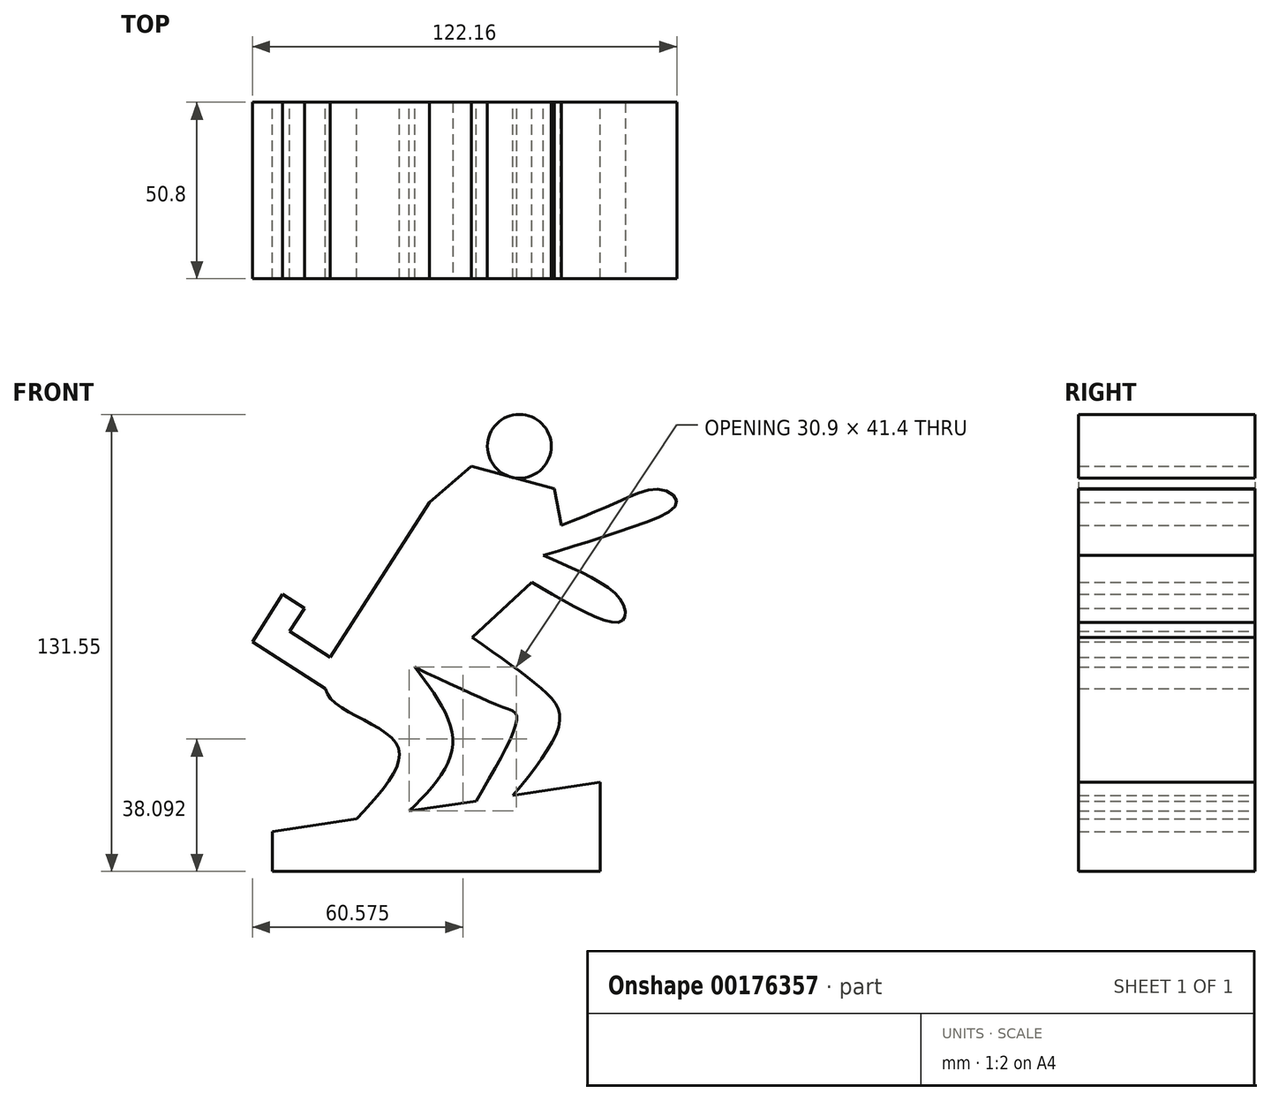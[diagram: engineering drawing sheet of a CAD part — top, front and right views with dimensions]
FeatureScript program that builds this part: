
annotation { "Feature Type Name" : "Feature", "Feature Type Description" : "" }
export const myFeature = defineFeature(function(context is Context, id is Id, definition is map)
    precondition{}
    {
        {
            var Q0;
            Q0=qCreatedBy(makeId("Front.planeOp"),FACE);
            var sketch = newSketch(context, id + "F0", { "sketchPlane" : qUnion([Q0])});
            skCircle(sketch, "E0", {"center": v(25.9, 46.62) * mm, "radius": 9.18 * mm});
            skLineSegment(sketch, "E1", {"start": v(12.09, 40.87) * mm, "end": v(35.96, 34.37) * mm});
            skLineSegment(sketch, "E2", {"start": v(12.09, 40.87) * mm, "end": v(0, 30.5) * mm});
            skLineSegment(sketch, "E3", {"start": v(0, 30.5) * mm, "end": v(-28.5, -14.1) * mm});
            skLineSegment(sketch, "E4", {"start": v(35.96, 34.37) * mm, "end": v(38, 23.89) * mm});
            skLineSegment(sketch, "E5", {"start": v(38, 23.89) * mm, "end": v(32.8, 15.25) * mm});
            skLineSegment(sketch, "E6", {"start": v(18.42, 23.89) * mm, "end": v(14.68, 15.25) * mm});
            skLineSegment(sketch, "E7", {"start": v(29.44, 7.54) * mm, "end": v(11.83, -8.81) * mm});
            skFitSpline(sketch, "E8", {"points": [v(-28.5, -14.1) * mm, v(-28.5, -25.9) * mm, v(-9.2, -39.43) * mm, v(-21.87, -61.62) * mm], "startDerivative": vector(-16.56, -48.93) * mm, "endDerivative": vector(-61.45, -65.14) * mm});
            skFitSpline(sketch, "E9", {"points": [v(18.42, 23.89) * mm, v(32.8, 15.25) * mm, v(54.97, 2.6) * mm, v(54.97, -3.84) * mm, v(29.44, 7.54) * mm, v(14.68, 15.25) * mm], "startDerivative": vector(63.22, -43.87) * mm, "endDerivative": vector(-62.95, 30.16) * mm});
            skFitSpline(sketch, "E10", {"points": [v(38, 23.89) * mm, v(53.97, 30.5) * mm, v(66.63, 34.22) * mm, v(71.24, 30.5) * mm, v(60.01, 23.89) * mm, v(32.8, 15.25) * mm], "startDerivative": vector(74.59, 29.4) * mm, "endDerivative": vector(-100.82, -30.07) * mm});
            skFitSpline(sketch, "E11", {"points": [v(0, 0) * mm, v(31.52, -22.48) * mm, v(37.56, -32.27) * mm, v(21.44, -57.02) * mm], "startDerivative": vector(88.18, -59.65) * mm, "endDerivative": vector(-64.62, -77.15) * mm});
            skFitSpline(sketch, "E12", {"points": [v(-13.67, -12.4) * mm, v(21.44, -28.52) * mm, v(25.19, -31.11) * mm, v(12.52, -57.02) * mm], "startDerivative": vector(94.72, -45.41) * mm, "endDerivative": vector(-50.43, -85.1) * mm});
            skFitSpline(sketch, "E13", {"points": [v(-4.18, -16.95) * mm, v(6.76, -39.43) * mm, v(-9.2, -61.62) * mm], "startDerivative": vector(35.42, -46.75) * mm, "endDerivative": vector(-44.95, -42.74) * mm});
            skLineSegment(sketch, "E14", {"start": v(-28.5, -14.1) * mm, "end": v(-40.17, -6.64) * mm});
            skLineSegment(sketch, "E15", {"start": v(-40.17, -6.64) * mm, "end": v(-35.93, 0) * mm});
            skLineSegment(sketch, "E16", {"start": v(-35.93, 0) * mm, "end": v(-42.2, 4.01) * mm});
            skLineSegment(sketch, "E17", {"start": v(-42.2, 4.01) * mm, "end": v(-50.92, -9.64) * mm});
            skLineSegment(sketch, "E18", {"start": v(-50.92, -9.64) * mm, "end": v(-29.91, -23.13) * mm});
            skLineSegment(sketch, "E19", {"start": v(-29.91, -23.13) * mm, "end": v(-32.1, -21.9) * mm});
            skLineSegment(sketch, "E20", {"start": v(-45.14, -64.27) * mm, "end": v(49.2, -50.06) * mm});
            skLineSegment(sketch, "E21", {"start": v(-45.14, -64.27) * mm, "end": v(-45.14, -75.74) * mm});
            skLineSegment(sketch, "E22", {"start": v(-45.14, -75.74) * mm, "end": v(49.2, -75.74) * mm});
            skLineSegment(sketch, "E23", {"start": v(49.2, -75.74) * mm, "end": v(49.2, -50.06) * mm});
            skSolve(sketch);
        }
        {
            var Q0;
            Q0 = qSketchRegion(id + "F0", true);
            extrude(context, id + "F1", {"entities" : qUnion([Q0]), "depth" : 50.8 * mm});
        }
    });
